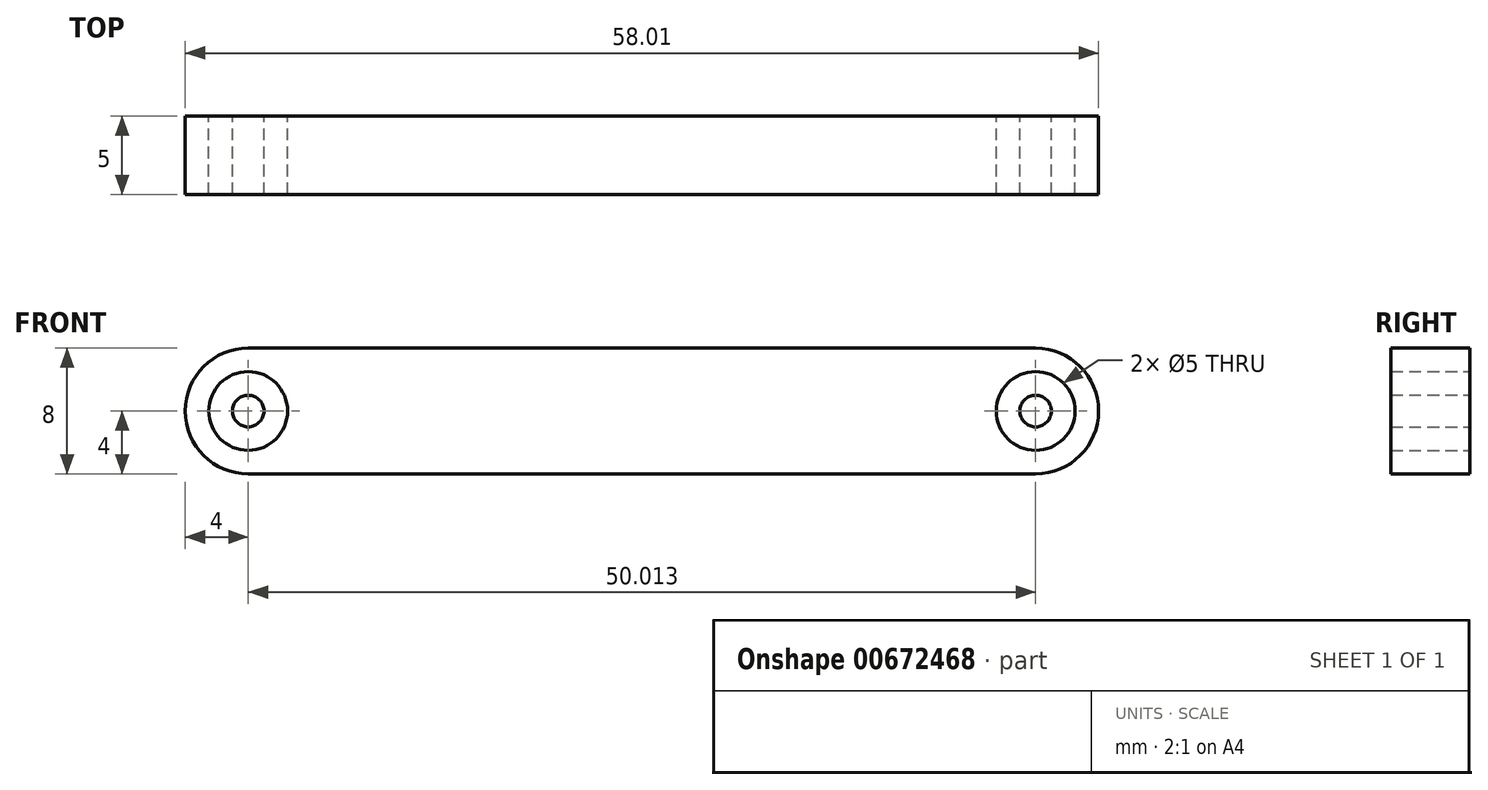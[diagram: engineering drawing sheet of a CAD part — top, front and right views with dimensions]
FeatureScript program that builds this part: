
annotation { "Feature Type Name" : "Feature", "Feature Type Description" : "" }
export const myFeature = defineFeature(function(context is Context, id is Id, definition is map)
    precondition{}
    {
        {
            var Q0;
            Q0=qCreatedBy(makeId("Front.planeOp"),FACE);
            var sketch = newSketch(context, id + "F0", { "sketchPlane" : qUnion([Q0])});
            skArc(sketch, "E0", {"start": v(0, 4) * mm, "mid": v(-4, 0) * mm, "end": v(0, -4) * mm});
            skCircle(sketch, "E1", {"center": v(0, 0) * mm, "radius": 2.5 * mm});
            skArc(sketch, "E2", {"start": v(50.01, -4) * mm, "mid": v(54.01, 0) * mm, "end": v(50.01, 4) * mm});
            skCircle(sketch, "E3", {"center": v(50.01, 0) * mm, "radius": 2.5 * mm});
            skLineSegment(sketch, "E4", {"start": v(0, 4) * mm, "end": v(50.01, 4) * mm});
            skLineSegment(sketch, "E5", {"start": v(0, -4) * mm, "end": v(50.01, -4) * mm});
            skCircle(sketch, "E6", {"center": v(0, 0) * mm, "radius": 1 * mm});
            skCircle(sketch, "E7", {"center": v(50.01, 0) * mm, "radius": 1 * mm});
            skSolve(sketch);
        }
        {
            var Q0;
            Q0=makeQuery(id+"F0.imprint","IMPRINT",FACE,{"disambiguationData":[TD([[makeQuery(id+"F0.imprint","IMPRINT",EDGE,{"derivedFrom":sQuery(id+"F0.wireOp",EDGE,"E0")}),1.0]])]});
            var Q1;
            Q1=makeQuery(id+"F0.imprint","IMPRINT",FACE,{"disambiguationData":[TD([[makeQuery(id+"F0.imprint","IMPRINT",EDGE,{"derivedFrom":sQuery(id+"F0.wireOp",EDGE,"E6")}),1.0]])]});
            var Q2;
            Q2=makeQuery(id+"F0.imprint","IMPRINT",FACE,{"disambiguationData":[TD([[makeQuery(id+"F0.imprint","IMPRINT",EDGE,{"derivedFrom":sQuery(id+"F0.wireOp",EDGE,"E7")}),1.0]])]});
            extrude(context, id + "F1", {"entities" : qUnion([Q0, Q1, Q2]), "endBound" : BoundingType.SYMMETRIC, "depth" : 5 * mm, "offsetDistance" : 25.4 * mm});
        }
    });
